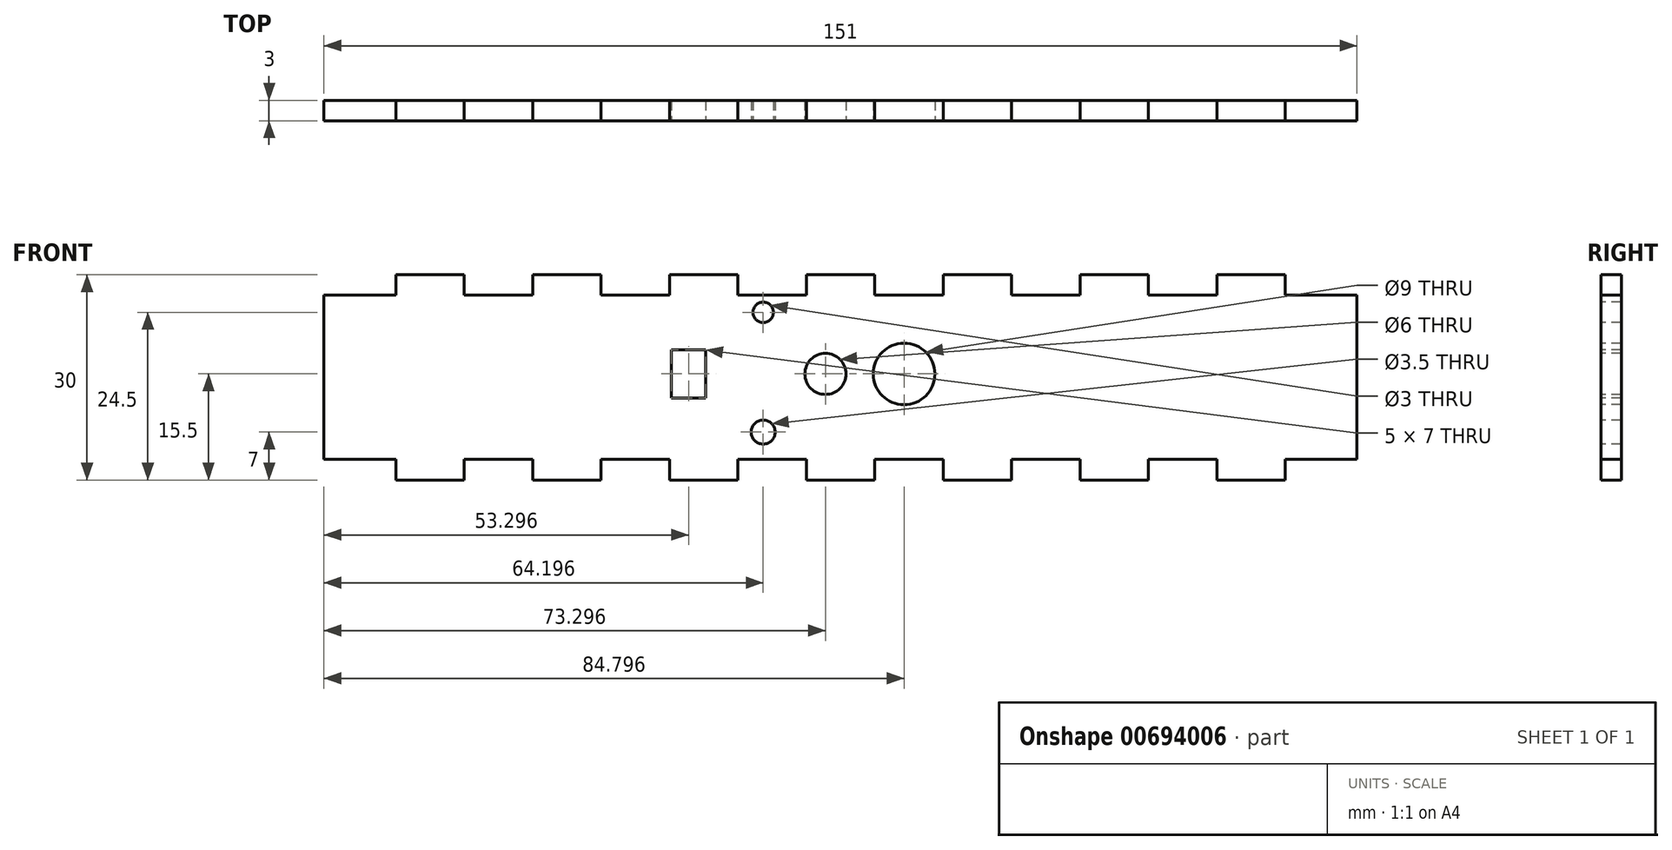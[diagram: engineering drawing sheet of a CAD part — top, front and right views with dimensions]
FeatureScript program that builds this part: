
annotation { "Feature Type Name" : "Feature", "Feature Type Description" : "" }
export const myFeature = defineFeature(function(context is Context, id is Id, definition is map)
    precondition{}
    {
        {
            var Q0;
            Q0=qCreatedBy(makeId("Front.planeOp"),FACE);
            var sketch = newSketch(context, id + "F0", { "sketchPlane" : qUnion([Q0])});
            skLineSegment(sketch, "E0.bottom", {"start": v(75.5, 15) * mm, "end": v(-75.5, 15) * mm});
            skLineSegment(sketch, "E0.top", {"start": v(75.5, -15) * mm, "end": v(-75.5, -15) * mm});
            skLineSegment(sketch, "E0.left", {"start": v(75.5, 15) * mm, "end": v(75.5, -15) * mm});
            skLineSegment(sketch, "E0.right", {"start": v(-75.5, 15) * mm, "end": v(-75.5, -15) * mm});
            skPoint(sketch, "E0.middle", {"position": v(0, 0) * mm});
            skSolve(sketch);
        }
        {
            var Q0;
            Q0=makeQuery(id+"F0.imprint","IMPRINT",FACE,{"disambiguationData":[TD([[makeQuery(id+"F0.imprint","IMPRINT",EDGE,{"derivedFrom":sQuery(id+"F0.wireOp",EDGE,"E0.bottom")}),1.0]])]});
            extrude(context, id + "F1", {"entities" : qUnion([Q0]), "depth" : 3 * mm, "offsetDistance" : 25 * mm});
        }
        {
            var Q0;
            Q0=makeQuery(id+"F1.opExtrude","CAP_FACE",FACE,{"disambiguationData":[OSD([sQuery(id+"F0.wireOp",EDGE,"E0.bottom"),sQuery(id+"F0.wireOp",EDGE,"E0.top"),sQuery(id+"F0.wireOp",EDGE,"E0.left"),sQuery(id+"F0.wireOp",EDGE,"E0.right")])],"isStart":false});
            var sketch = newSketch(context, id + "F2", { "sketchPlane" : qUnion([Q0])});
            skLineSegment(sketch, "E1.bottom", {"start": v(-75, -15) * mm, "end": v(-65, -15) * mm});
            skLineSegment(sketch, "E1.top", {"start": v(-75, -12) * mm, "end": v(-65, -12) * mm});
            skLineSegment(sketch, "E1.left", {"start": v(-75, -15) * mm, "end": v(-75, -12) * mm});
            skLineSegment(sketch, "E1.right", {"start": v(-65, -15) * mm, "end": v(-65, -12) * mm});
            skLineSegment(sketch, "E2.0.1.0", {"start": v(-75, 12) * mm, "end": v(-65, 12) * mm});
            skLineSegment(sketch, "E2.0.1.1", {"start": v(-75, 15) * mm, "end": v(-65, 15) * mm});
            skLineSegment(sketch, "E2.0.1.2", {"start": v(-75, 12) * mm, "end": v(-75, 15) * mm});
            skLineSegment(sketch, "E2.0.1.3", {"start": v(-65, 12) * mm, "end": v(-65, 15) * mm});
            skLineSegment(sketch, "E2.1.0.0", {"start": v(-55, -15) * mm, "end": v(-45, -15) * mm});
            skLineSegment(sketch, "E2.1.0.1", {"start": v(-55, -12) * mm, "end": v(-45, -12) * mm});
            skLineSegment(sketch, "E2.1.0.2", {"start": v(-55, -15) * mm, "end": v(-55, -12) * mm});
            skLineSegment(sketch, "E2.1.0.3", {"start": v(-45, -15) * mm, "end": v(-45, -12) * mm});
            skLineSegment(sketch, "E2.1.1.0", {"start": v(-55, 12) * mm, "end": v(-45, 12) * mm});
            skLineSegment(sketch, "E2.1.1.1", {"start": v(-55, 15) * mm, "end": v(-45, 15) * mm});
            skLineSegment(sketch, "E2.1.1.2", {"start": v(-55, 12) * mm, "end": v(-55, 15) * mm});
            skLineSegment(sketch, "E2.1.1.3", {"start": v(-45, 12) * mm, "end": v(-45, 15) * mm});
            skLineSegment(sketch, "E2.2.0.0", {"start": v(-35, -15) * mm, "end": v(-25, -15) * mm});
            skLineSegment(sketch, "E2.2.0.1", {"start": v(-35, -12) * mm, "end": v(-25, -12) * mm});
            skLineSegment(sketch, "E2.2.0.2", {"start": v(-35, -15) * mm, "end": v(-35, -12) * mm});
            skLineSegment(sketch, "E2.2.0.3", {"start": v(-25, -15) * mm, "end": v(-25, -12) * mm});
            skLineSegment(sketch, "E2.2.1.0", {"start": v(-35, 12) * mm, "end": v(-25, 12) * mm});
            skLineSegment(sketch, "E2.2.1.1", {"start": v(-35, 15) * mm, "end": v(-25, 15) * mm});
            skLineSegment(sketch, "E2.2.1.2", {"start": v(-35, 12) * mm, "end": v(-35, 15) * mm});
            skLineSegment(sketch, "E2.2.1.3", {"start": v(-25, 12) * mm, "end": v(-25, 15) * mm});
            skLineSegment(sketch, "E2.3.0.0", {"start": v(-15, -15) * mm, "end": v(-5, -15) * mm});
            skLineSegment(sketch, "E2.3.0.1", {"start": v(-15, -12) * mm, "end": v(-5, -12) * mm});
            skLineSegment(sketch, "E2.3.0.2", {"start": v(-15, -15) * mm, "end": v(-15, -12) * mm});
            skLineSegment(sketch, "E2.3.0.3", {"start": v(-5, -15) * mm, "end": v(-5, -12) * mm});
            skLineSegment(sketch, "E2.3.1.0", {"start": v(-15, 12) * mm, "end": v(-5, 12) * mm});
            skLineSegment(sketch, "E2.3.1.1", {"start": v(-15, 15) * mm, "end": v(-5, 15) * mm});
            skLineSegment(sketch, "E2.3.1.2", {"start": v(-15, 12) * mm, "end": v(-15, 15) * mm});
            skLineSegment(sketch, "E2.3.1.3", {"start": v(-5, 12) * mm, "end": v(-5, 15) * mm});
            skLineSegment(sketch, "E2.4.0.0", {"start": v(5, -15) * mm, "end": v(15, -15) * mm});
            skLineSegment(sketch, "E2.4.0.1", {"start": v(5, -12) * mm, "end": v(15, -12) * mm});
            skLineSegment(sketch, "E2.4.0.2", {"start": v(5, -15) * mm, "end": v(5, -12) * mm});
            skLineSegment(sketch, "E2.4.0.3", {"start": v(15, -15) * mm, "end": v(15, -12) * mm});
            skLineSegment(sketch, "E2.4.1.0", {"start": v(5, 12) * mm, "end": v(15, 12) * mm});
            skLineSegment(sketch, "E2.4.1.1", {"start": v(5, 15) * mm, "end": v(15, 15) * mm});
            skLineSegment(sketch, "E2.4.1.2", {"start": v(5, 12) * mm, "end": v(5, 15) * mm});
            skLineSegment(sketch, "E2.4.1.3", {"start": v(15, 12) * mm, "end": v(15, 15) * mm});
            skLineSegment(sketch, "E2.5.0.0", {"start": v(25, -15) * mm, "end": v(35, -15) * mm});
            skLineSegment(sketch, "E2.5.0.1", {"start": v(25, -12) * mm, "end": v(35, -12) * mm});
            skLineSegment(sketch, "E2.5.0.2", {"start": v(25, -15) * mm, "end": v(25, -12) * mm});
            skLineSegment(sketch, "E2.5.0.3", {"start": v(35, -15) * mm, "end": v(35, -12) * mm});
            skLineSegment(sketch, "E2.5.1.0", {"start": v(25, 12) * mm, "end": v(35, 12) * mm});
            skLineSegment(sketch, "E2.5.1.1", {"start": v(25, 15) * mm, "end": v(35, 15) * mm});
            skLineSegment(sketch, "E2.5.1.2", {"start": v(25, 12) * mm, "end": v(25, 15) * mm});
            skLineSegment(sketch, "E2.5.1.3", {"start": v(35, 12) * mm, "end": v(35, 15) * mm});
            skLineSegment(sketch, "E2.6.0.0", {"start": v(45, -15) * mm, "end": v(55, -15) * mm});
            skLineSegment(sketch, "E2.6.0.1", {"start": v(45, -12) * mm, "end": v(55, -12) * mm});
            skLineSegment(sketch, "E2.6.0.2", {"start": v(45, -15) * mm, "end": v(45, -12) * mm});
            skLineSegment(sketch, "E2.6.0.3", {"start": v(55, -15) * mm, "end": v(55, -12) * mm});
            skLineSegment(sketch, "E2.6.1.0", {"start": v(45, 12) * mm, "end": v(55, 12) * mm});
            skLineSegment(sketch, "E2.6.1.1", {"start": v(45, 15) * mm, "end": v(55, 15) * mm});
            skLineSegment(sketch, "E2.6.1.2", {"start": v(45, 12) * mm, "end": v(45, 15) * mm});
            skLineSegment(sketch, "E2.6.1.3", {"start": v(55, 12) * mm, "end": v(55, 15) * mm});
            skLineSegment(sketch, "E2.7.0.0", {"start": v(65, -15) * mm, "end": v(75, -15) * mm});
            skLineSegment(sketch, "E2.7.0.1", {"start": v(65, -12) * mm, "end": v(75, -12) * mm});
            skLineSegment(sketch, "E2.7.0.2", {"start": v(65, -15) * mm, "end": v(65, -12) * mm});
            skLineSegment(sketch, "E2.7.0.3", {"start": v(75, -15) * mm, "end": v(75, -12) * mm});
            skLineSegment(sketch, "E2.7.1.0", {"start": v(65, 12) * mm, "end": v(75, 12) * mm});
            skLineSegment(sketch, "E2.7.1.1", {"start": v(65, 15) * mm, "end": v(75, 15) * mm});
            skLineSegment(sketch, "E2.7.1.2", {"start": v(65, 12) * mm, "end": v(65, 15) * mm});
            skLineSegment(sketch, "E2.7.1.3", {"start": v(75, 12) * mm, "end": v(75, 15) * mm});
            skLineSegment(sketch, "E2.direction1", {"start": v(-75, -15) * mm, "end": v(-55, -15) * mm, "construction": true});
            skLineSegment(sketch, "E2.direction2", {"start": v(-75, -15) * mm, "end": v(-75, 12) * mm, "construction": true});
            skLineSegment(sketch, "E3.bottom", {"start": v(-70, 12) * mm, "end": v(-81.45, 12) * mm});
            skLineSegment(sketch, "E3.top", {"start": v(-70, 15) * mm, "end": v(-81.45, 15) * mm});
            skLineSegment(sketch, "E3.left", {"start": v(-70, 12) * mm, "end": v(-70, 15) * mm});
            skLineSegment(sketch, "E3.right", {"start": v(-81.45, 12) * mm, "end": v(-81.45, 15) * mm});
            skLineSegment(sketch, "E4.0.1.0", {"start": v(-70, -15) * mm, "end": v(-70, -12) * mm});
            skLineSegment(sketch, "E4.0.1.1", {"start": v(-81.45, -15) * mm, "end": v(-81.45, -12) * mm});
            skLineSegment(sketch, "E4.0.1.2", {"start": v(-70, -12) * mm, "end": v(-81.45, -12) * mm});
            skLineSegment(sketch, "E4.0.1.3", {"start": v(-70, -15) * mm, "end": v(-81.45, -15) * mm});
            skLineSegment(sketch, "E4.1.0.0", {"start": v(80, 12) * mm, "end": v(80, 15) * mm});
            skLineSegment(sketch, "E4.1.0.1", {"start": v(68.55, 12) * mm, "end": v(68.55, 15) * mm});
            skLineSegment(sketch, "E4.1.0.2", {"start": v(80, 15) * mm, "end": v(68.55, 15) * mm});
            skLineSegment(sketch, "E4.1.0.3", {"start": v(80, 12) * mm, "end": v(68.55, 12) * mm});
            skLineSegment(sketch, "E4.1.1.0", {"start": v(80, -15) * mm, "end": v(80, -12) * mm});
            skLineSegment(sketch, "E4.1.1.1", {"start": v(68.55, -15) * mm, "end": v(68.55, -12) * mm});
            skLineSegment(sketch, "E4.1.1.2", {"start": v(80, -12) * mm, "end": v(68.55, -12) * mm});
            skLineSegment(sketch, "E4.1.1.3", {"start": v(80, -15) * mm, "end": v(68.55, -15) * mm});
            skLineSegment(sketch, "E4.direction1", {"start": v(-81.45, 12) * mm, "end": v(68.55, 12) * mm, "construction": true});
            skLineSegment(sketch, "E4.direction2", {"start": v(-81.45, 12) * mm, "end": v(-81.45, -15) * mm, "construction": true});
            skCircle(sketch, "E5", {"center": v(9.3, 0.5) * mm, "radius": 4.5 * mm});
            skCircle(sketch, "E6", {"center": v(-11.3, 9.5) * mm, "radius": 1.5 * mm});
            skCircle(sketch, "E7", {"center": v(-11.3, -8) * mm, "radius": 1.75 * mm});
            skCircle(sketch, "E8", {"center": v(-2.2, 0.5) * mm, "radius": 3 * mm});
            skLineSegment(sketch, "E9.bottom", {"start": v(-24.7, -3) * mm, "end": v(-19.7, -3) * mm});
            skLineSegment(sketch, "E9.top", {"start": v(-24.7, 4) * mm, "end": v(-19.7, 4) * mm});
            skLineSegment(sketch, "E9.left", {"start": v(-24.7, -3) * mm, "end": v(-24.7, 4) * mm});
            skLineSegment(sketch, "E9.right", {"start": v(-19.7, -3) * mm, "end": v(-19.7, 4) * mm});
            skPoint(sketch, "E9.middle", {"position": v(-22.2, 0.5) * mm});
            skSolve(sketch);
        }
        {
            var Q0;
            Q0 = qSketchRegion(id + "F2", true);
            extrude(context, id + "F3", {"entities" : qUnion([Q0]), "operationType" : NewBodyOperationType.REMOVE, "oppositeDirection" : true, "depth" : 25 * mm, "offsetDistance" : 25 * mm});
        }
    });
